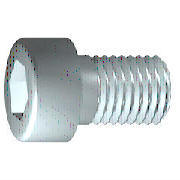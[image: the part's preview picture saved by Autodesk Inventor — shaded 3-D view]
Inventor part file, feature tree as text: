
AUTODESK INVENTOR PART (.ipt)
format: ipt  version: 2024.3 (Build 283343000, 343)  size: 190,464 bytes
history: native  units: mm (DEFAULTED — no unit token found)
features: extrude x1, plane x1, fillet x1
ambient origin geometry x7: Origin, YZ Plane, XY Plane, X Axis, Y Axis, Z Axis, Center Point
bodies: Solid1 (feature_tree), Body (feature_tree)
feature tree (3):
  extrude  "Slot"  Depth=14.75mm
  plane  "Work Plane1"
  fillet  "Fillet2"  Radius=0.306825mm
